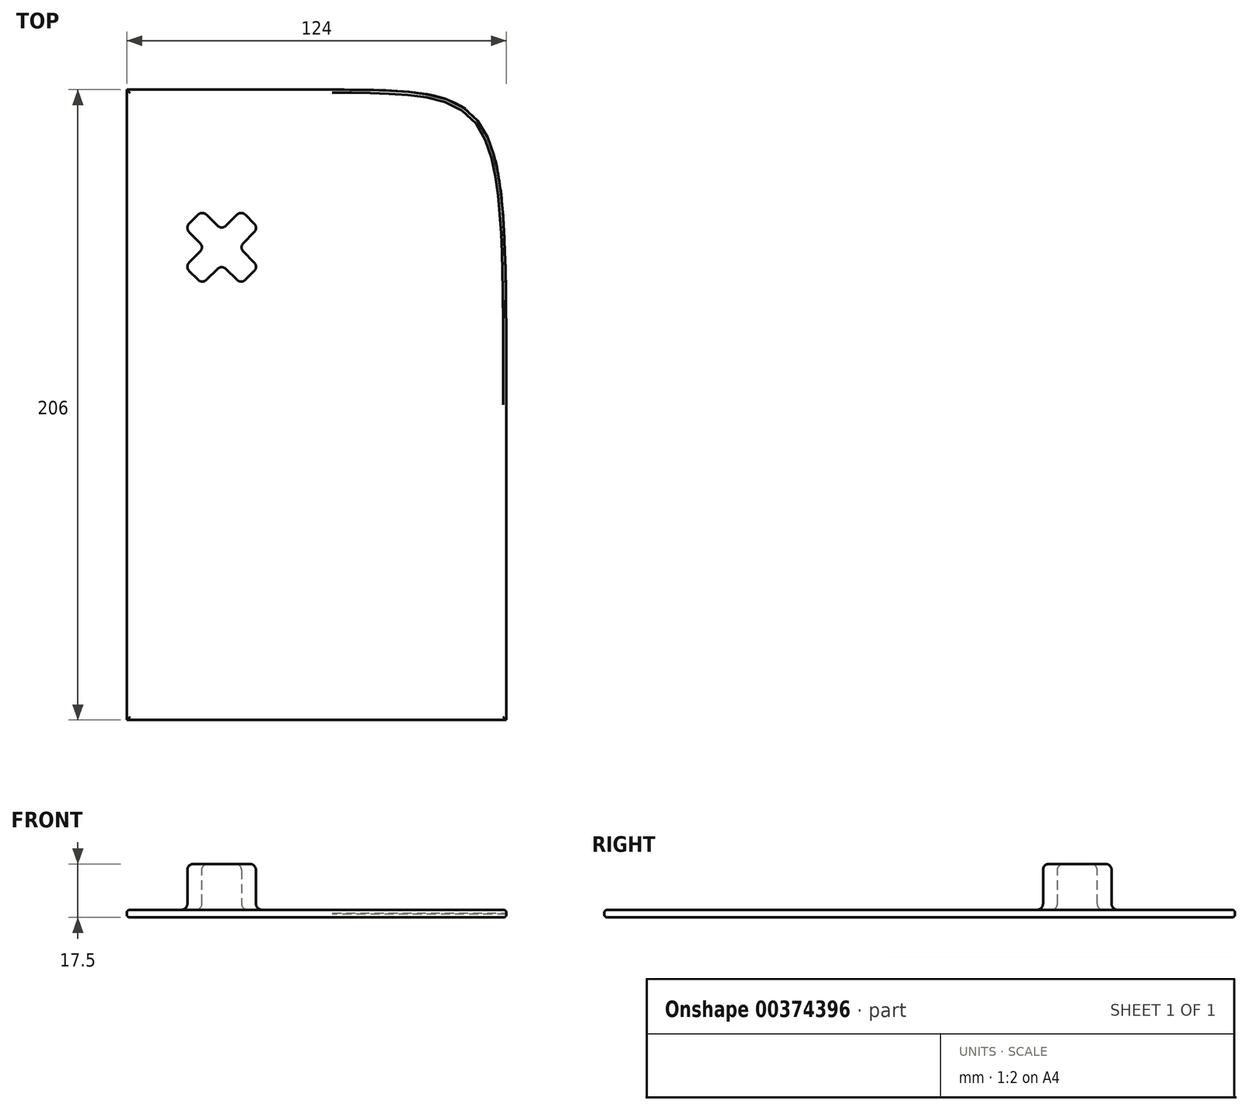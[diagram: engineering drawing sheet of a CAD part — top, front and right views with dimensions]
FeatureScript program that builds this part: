
annotation { "Feature Type Name" : "Feature", "Feature Type Description" : "" }
export const myFeature = defineFeature(function(context is Context, id is Id, definition is map)
    precondition{}
    {
        {
            var Q0;
            Q0=qCreatedBy(makeId("Top.planeOp"),FACE);
            var sketch = newSketch(context, id + "F0", { "sketchPlane" : qUnion([Q0])});
            skLineSegment(sketch, "E0.bottom", {"start": v(62, 103) * mm, "end": v(-62, 103) * mm});
            skLineSegment(sketch, "E0.top", {"start": v(62, -103) * mm, "end": v(-62, -103) * mm});
            skLineSegment(sketch, "E0.left", {"start": v(62, 103) * mm, "end": v(62, -103) * mm});
            skLineSegment(sketch, "E0.right", {"start": v(-62, 103) * mm, "end": v(-62, -103) * mm});
            skPoint(sketch, "E0.middle", {"position": v(0, 0) * mm});
            skSolve(sketch);
        }
        {
            var Q0;
            Q0 = qSketchRegion(id + "F0", true);
            extrude(context, id + "F1", {"entities" : qUnion([Q0]), "depth" : 2.5 * mm});
        }
        {
            var Q0;
            Q0=makeQuery(id+"F1.opExtrude","CAP_FACE",FACE,{"disambiguationData":[OSD([sQuery(id+"F0.wireOp",EDGE,"E0.bottom"),sQuery(id+"F0.wireOp",EDGE,"E0.top"),sQuery(id+"F0.wireOp",EDGE,"E0.left"),sQuery(id+"F0.wireOp",EDGE,"E0.right")])],"isStart":false});
            var sketch = newSketch(context, id + "F2", { "sketchPlane" : qUnion([Q0])});
            skLineSegment(sketch, "E1", {"start": v(0, 0) * mm, "end": v(0, 103) * mm, "construction": true});
            skLineSegment(sketch, "E2", {"start": v(0, 0) * mm, "end": v(62, 0) * mm, "construction": true});
            skPoint(sketch, "E3.orphan", {"position": v(-62, 103) * mm});
            skFitSpline(sketch, "E4", {"points": [v(0, 103) * mm, v(62, 0) * mm], "startDerivative": vector(186, 0) * mm, "endDerivative": vector(0, -312) * mm});
            skLineSegment(sketch, "E5", {"start": v(0, 103) * mm, "end": v(62, 103) * mm});
            skLineSegment(sketch, "E6", {"start": v(62, 0) * mm, "end": v(62, 104) * mm});
            skSolve(sketch);
        }
        {
            var Q0;
            Q0 = qSketchRegion(id + "F2", true);
            extrude(context, id + "F3", {"entities" : qUnion([Q0]), "operationType" : NewBodyOperationType.REMOVE, "endBound" : BoundingType.THROUGH_ALL, "oppositeDirection" : true, "depth" : 25 * mm});
        }
        {
            var Q0;
            Q0=makeQuery(id+"F1.opExtrude","CAP_FACE",FACE,{"disambiguationData":[OSD([sQuery(id+"F0.wireOp",EDGE,"E0.bottom"),sQuery(id+"F0.wireOp",EDGE,"E0.top"),sQuery(id+"F0.wireOp",EDGE,"E0.left"),sQuery(id+"F0.wireOp",EDGE,"E0.right")])],"isStart":false});
            var sketch = newSketch(context, id + "F4", { "sketchPlane" : qUnion([Q0])});
            skLineSegment(sketch, "E7", {"start": v(0, 0) * mm, "end": v(0, 103) * mm, "construction": true});
            skPoint(sketch, "E8.endSnap0", {"position": v(0, 51.5) * mm});
            skLineSegment(sketch, "E9", {"start": v(-62, 0) * mm, "end": v(-62, 103) * mm, "construction": true});
            skLineSegment(sketch, "E10", {"start": v(0, 51.5) * mm, "end": v(-62, 51.5) * mm, "construction": true});
            skLineSegment(sketch, "E11", {"start": v(-31, 51.5) * mm, "end": v(-21.8, 60.7) * mm, "construction": true});
            skLineSegment(sketch, "E12", {"start": v(-31, 51.5) * mm, "end": v(-40.2, 60.7) * mm, "construction": true});
            skLineSegment(sketch, "E13", {"start": v(-31, 51.5) * mm, "end": v(-40.2, 42.3) * mm, "construction": true});
            skLineSegment(sketch, "E14", {"start": v(-31, 51.5) * mm, "end": v(-21.8, 42.3) * mm, "construction": true});
            skLineSegment(sketch, "E15", {"start": v(-40.2, 60.7) * mm, "end": v(-43.02, 57.86) * mm});
            skLineSegment(sketch, "E16", {"start": v(-43.02, 57.86) * mm, "end": v(-36.66, 51.5) * mm});
            skLineSegment(sketch, "E17", {"start": v(-36.66, 51.5) * mm, "end": v(-43.02, 45.14) * mm});
            skLineSegment(sketch, "E18", {"start": v(-40.2, 42.3) * mm, "end": v(-43.02, 45.14) * mm});
            skLineSegment(sketch, "E19", {"start": v(-40.2, 42.3) * mm, "end": v(-37.36, 39.48) * mm});
            skLineSegment(sketch, "E20", {"start": v(-21.8, 42.3) * mm, "end": v(-24.64, 39.48) * mm});
            skLineSegment(sketch, "E21", {"start": v(-21.8, 42.3) * mm, "end": v(-18.98, 45.14) * mm});
            skLineSegment(sketch, "E22", {"start": v(-24.64, 39.48) * mm, "end": v(-31, 45.84) * mm});
            skLineSegment(sketch, "E23", {"start": v(-31, 45.84) * mm, "end": v(-37.36, 39.48) * mm});
            skLineSegment(sketch, "E24", {"start": v(-18.98, 45.14) * mm, "end": v(-25.34, 51.5) * mm});
            skLineSegment(sketch, "E25", {"start": v(-21.8, 60.7) * mm, "end": v(-24.64, 63.52) * mm});
            skLineSegment(sketch, "E26", {"start": v(-21.8, 60.7) * mm, "end": v(-18.98, 57.86) * mm});
            skLineSegment(sketch, "E27", {"start": v(-18.98, 57.86) * mm, "end": v(-25.34, 51.5) * mm});
            skLineSegment(sketch, "E28", {"start": v(-24.64, 63.52) * mm, "end": v(-31, 57.16) * mm});
            skLineSegment(sketch, "E29", {"start": v(-31, 57.16) * mm, "end": v(-37.36, 63.52) * mm});
            skLineSegment(sketch, "E30", {"start": v(-37.36, 63.52) * mm, "end": v(-40.2, 60.7) * mm});
            skSolve(sketch);
        }
        {
            var Q0;
            Q0 = qSketchRegion(id + "F4", true);
            extrude(context, id + "F5", {"entities" : qUnion([Q0]), "operationType" : NewBodyOperationType.ADD, "depth" : 15 * mm});
        }
        {
            var Q0;
            Q0=makeQuery(id+"F5.opExtrude","SWEPT_FACE",FACE,{"disambiguationData":[OSD([sQuery(id+"F4.wireOp",EDGE,"E23")])]});
            var Q1;
            Q1=makeQuery(id+"F5.opExtrude","SWEPT_FACE",FACE,{"disambiguationData":[OSD([sQuery(id+"F4.wireOp",EDGE,"E22")])]});
            var Q2;
            Q2=makeQuery(id+"F5.opExtrude","SWEPT_FACE",FACE,{"disambiguationData":[OSD([sQuery(id+"F4.wireOp",EDGE,"E20"),sQuery(id+"F4.wireOp",EDGE,"E21")])]});
            var Q3;
            Q3=makeQuery(id+"F5.opExtrude","SWEPT_FACE",FACE,{"disambiguationData":[OSD([sQuery(id+"F4.wireOp",EDGE,"E18"),sQuery(id+"F4.wireOp",EDGE,"E19")])]});
            var Q4;
            Q4=makeQuery(id+"F5.opExtrude","SWEPT_FACE",FACE,{"disambiguationData":[OSD([sQuery(id+"F4.wireOp",EDGE,"E17")])]});
            var Q5;
            Q5=makeQuery(id+"F5.opExtrude","SWEPT_FACE",FACE,{"disambiguationData":[OSD([sQuery(id+"F4.wireOp",EDGE,"E16")])]});
            var Q6;
            Q6=makeQuery(id+"F5.opExtrude","SWEPT_FACE",FACE,{"disambiguationData":[OSD([sQuery(id+"F4.wireOp",EDGE,"E15"),sQuery(id+"F4.wireOp",EDGE,"E30")])]});
            var Q7;
            Q7=makeQuery(id+"F5.opExtrude","SWEPT_FACE",FACE,{"disambiguationData":[OSD([sQuery(id+"F4.wireOp",EDGE,"E29")])]});
            var Q8;
            Q8=makeQuery(id+"F5.opExtrude","SWEPT_FACE",FACE,{"disambiguationData":[OSD([sQuery(id+"F4.wireOp",EDGE,"E28")])]});
            var Q9;
            Q9=makeQuery(id+"F5.opExtrude","SWEPT_FACE",FACE,{"disambiguationData":[OSD([sQuery(id+"F4.wireOp",EDGE,"E25"),sQuery(id+"F4.wireOp",EDGE,"E26")])]});
            var Q10;
            Q10=makeQuery(id+"F5.opExtrude","SWEPT_FACE",FACE,{"disambiguationData":[OSD([sQuery(id+"F4.wireOp",EDGE,"E27")])]});
            var Q11;
            Q11=makeQuery(id+"F5.opExtrude","SWEPT_FACE",FACE,{"disambiguationData":[OSD([sQuery(id+"F4.wireOp",EDGE,"E24")])]});
            fillet(context, id + "F6", {"entities" : qUnion([Q0, Q1, Q2, Q3, Q4, Q5, Q6, Q7, Q8, Q9, Q10, Q11]), "radius" : 2 * mm, "tangentPropagation" : true, "allowEdgeOverflow" : false});
        }
        {
            var Q0;
            Q0=makeQuery(id+"F1.opExtrude","CAP_FACE",FACE,{"disambiguationData":[OSD([sQuery(id+"F0.wireOp",EDGE,"E0.bottom"),sQuery(id+"F0.wireOp",EDGE,"E0.top"),sQuery(id+"F0.wireOp",EDGE,"E0.left"),sQuery(id+"F0.wireOp",EDGE,"E0.right")])],"isStart":true});
            var Q1;
            Q1=makeQuery(id+"F1.opExtrude","CAP_FACE",FACE,{"disambiguationData":[OSD([sQuery(id+"F0.wireOp",EDGE,"E0.bottom"),sQuery(id+"F0.wireOp",EDGE,"E0.top"),sQuery(id+"F0.wireOp",EDGE,"E0.left"),sQuery(id+"F0.wireOp",EDGE,"E0.right")])],"isStart":false});
            fillet(context, id + "F7", {"entities" : qUnion([Q0, Q1]), "radius" : 1 * mm, "tangentPropagation" : true, "allowEdgeOverflow" : false});
        }
    });
